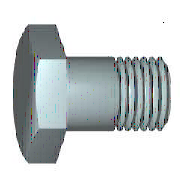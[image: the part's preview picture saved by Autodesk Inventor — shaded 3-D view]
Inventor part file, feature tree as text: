
AUTODESK INVENTOR PART (.ipt)
format: ipt  version: 2020 (Build 240168000, 168)  size: 199,168 bytes
history: native  units: mm (DEFAULTED — no unit token found)
features: sketch x4, other x4, plane x3, chamfer x1, fillet x1
ambient origin geometry x6: Origin, XY Plane, X Axis, Y Axis, Z Axis, Center Point
bodies: Solid1 (feature_tree)
feature tree (13):
  plane  "WorkPlane1"
  sketch  "Sketch1"  dims[d0=30.0mm]
  other  "WorkPoint1"
  chamfer  "Chamfer1"  Distance=5.3mm
  fillet  "Fillet1"  [1 undecoded]
  other  "MSC_A1"
  other  "MSC_PF1"
  other  "MSC_PT1"
  plane  "WorkPlane2"
  plane  "WorkPlane3"
  sketch  "Sketch2"  dims[d1=13.0mm]
  sketch  "Sketch3"  dims[d2=15.0mm]
  sketch  "Sketch4"  dims[d4=17.321016mm d6=5.3mm d7=0.0mm d8=15.0mm d10=0.0mm d12=30.0deg d14=360.0deg d15=0.0mm d17=10.0mm d18=4.0mm d19=80.0mm d20=40.0mm d21=360.0deg d22=0.625mm d23=0.625mm d24=0.4mm d25=0.1mm d26=0.0mm d27=60.0deg d28=6.5mm d29=0.0mm d30=0.0mm d32=0.0mm d33=0.0mm d34=0.0mm d37=0.0mm d38=0.0mm d39=45.0deg d40=0.0mm d41=0.0mm d42=0.0mm]
note: 1 required parameter value undecoded (feature->parameter linkage not recoverable at this tier; creation-order binding heuristic only, values carry confidence <= 0.55)
